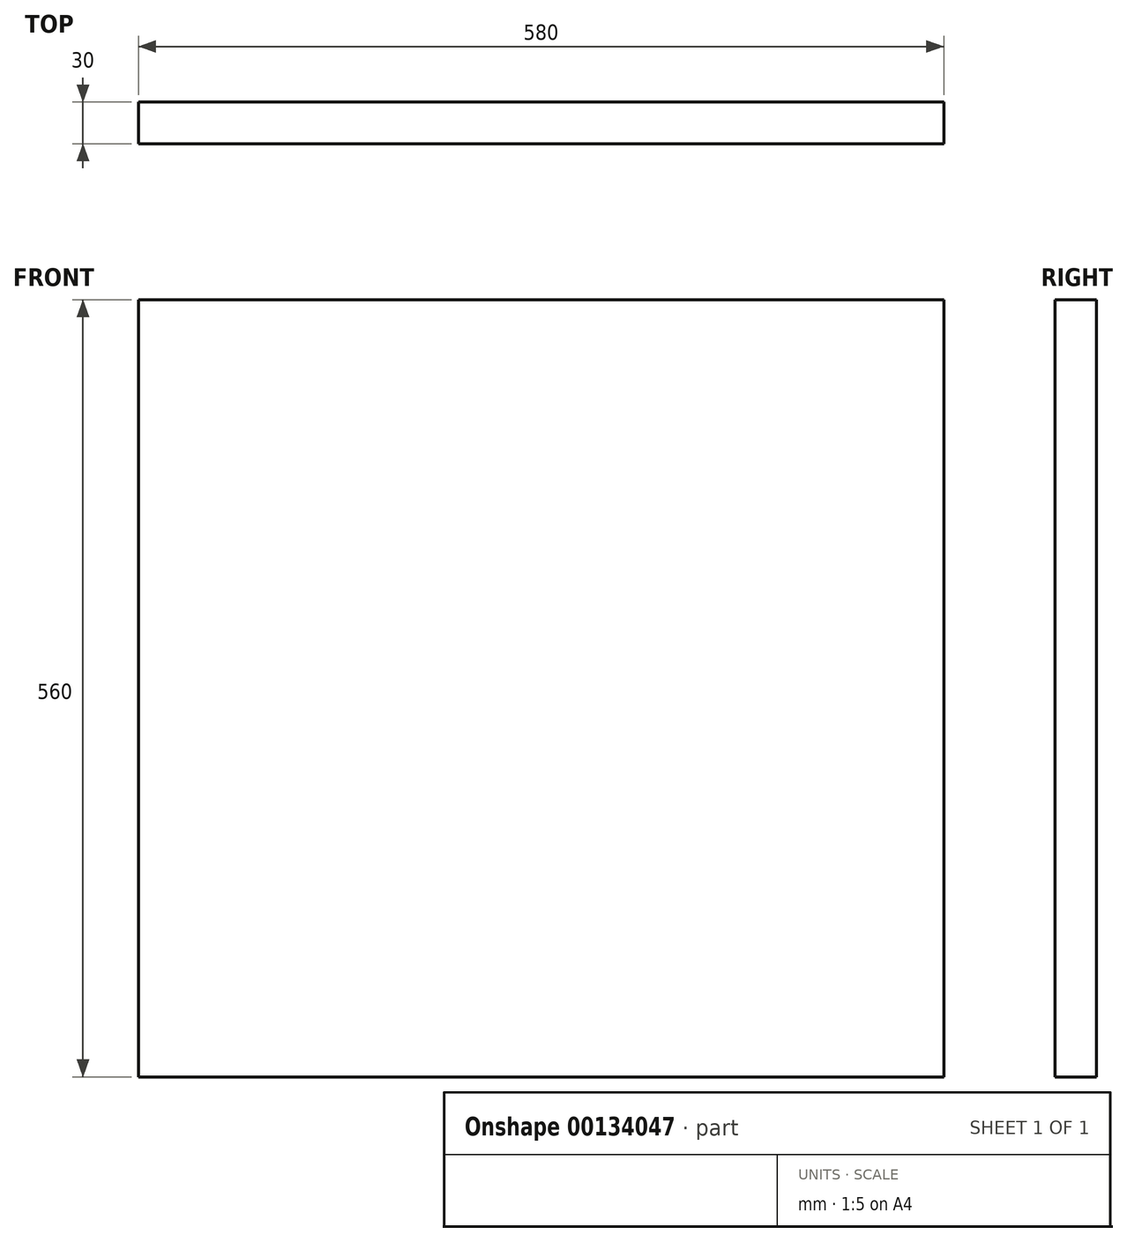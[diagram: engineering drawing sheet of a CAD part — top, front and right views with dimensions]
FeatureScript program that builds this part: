
annotation { "Feature Type Name" : "Feature", "Feature Type Description" : "" }
export const myFeature = defineFeature(function(context is Context, id is Id, definition is map)
    precondition{}
    {
        {
            var Q0;
            Q0=qCreatedBy(makeId("Front.planeOp"),FACE);
            var sketch = newSketch(context, id + "F0", { "sketchPlane" : qUnion([Q0])});
            skLineSegment(sketch, "E0.bottom", {"start": v(0, 0) * mm, "end": v(580, 0) * mm});
            skLineSegment(sketch, "E0.top", {"start": v(0, 560) * mm, "end": v(580, 560) * mm});
            skLineSegment(sketch, "E0.left", {"start": v(0, 0) * mm, "end": v(0, 560) * mm});
            skLineSegment(sketch, "E0.right", {"start": v(580, 0) * mm, "end": v(580, 560) * mm});
            skSolve(sketch);
        }
        {
            var Q0;
            Q0=makeQuery(id+"F0.imprint","IMPRINT",FACE,{"disambiguationData":[TD([[makeQuery(id+"F0.imprint","IMPRINT",EDGE,{"derivedFrom":sQuery(id+"F0.wireOp",EDGE,"E0.bottom")}),1.0]])]});
            extrude(context, id + "F1", {"entities" : qUnion([Q0]), "depth" : 30 * mm});
        }
    });
